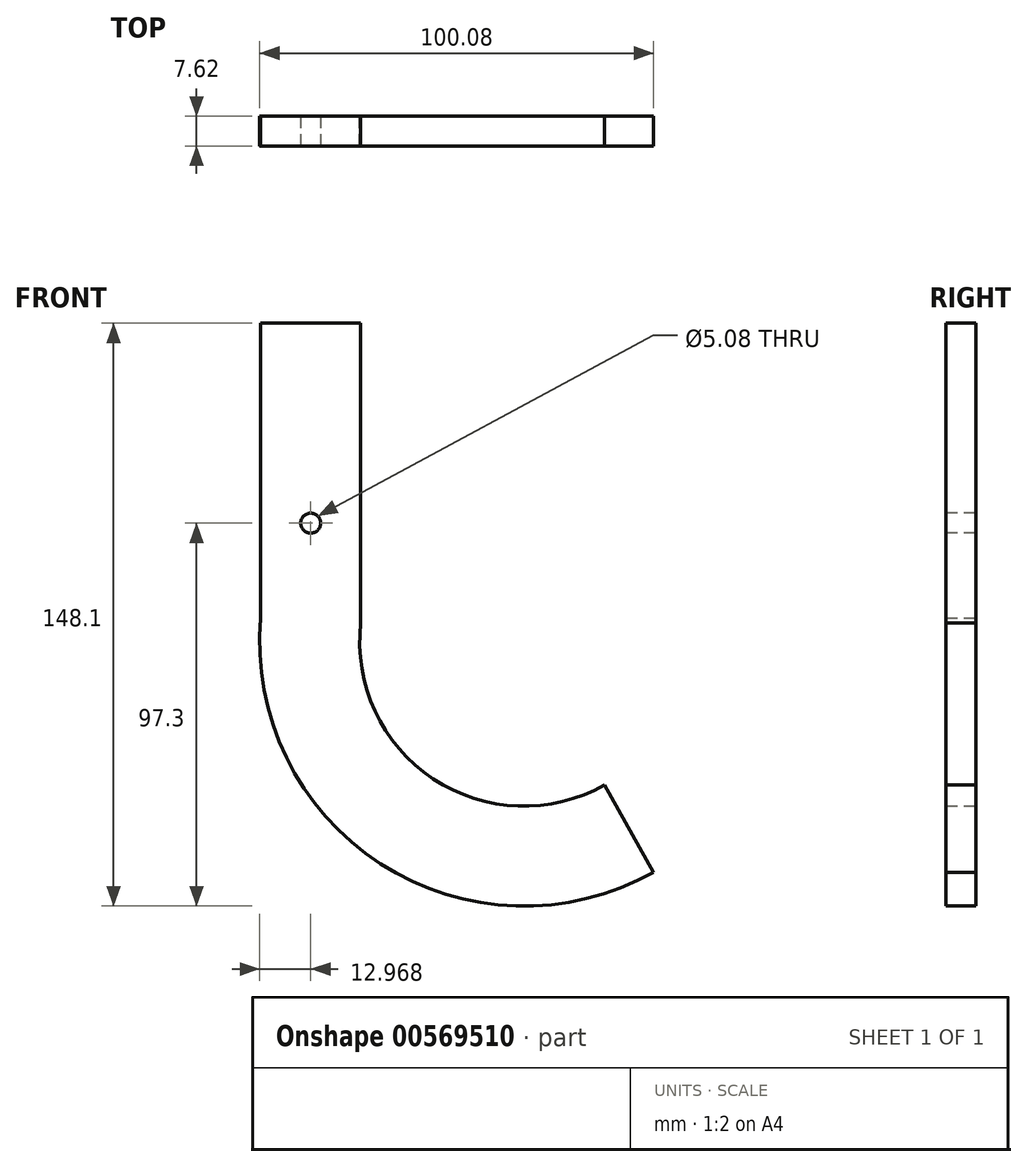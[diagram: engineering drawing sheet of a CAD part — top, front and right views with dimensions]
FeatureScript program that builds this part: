
annotation { "Feature Type Name" : "Feature", "Feature Type Description" : "" }
export const myFeature = defineFeature(function(context is Context, id is Id, definition is map)
    precondition{}
    {
        {
            var Q0;
            Q0=qCreatedBy(makeId("Front.planeOp"),FACE);
            var sketch = newSketch(context, id + "F0", { "sketchPlane" : qUnion([Q0])});
            skLineSegment(sketch, "E0", {"start": v(-8.68, 20.1) * mm, "end": v(-34.08, 20.1) * mm});
            skLineSegment(sketch, "E1.bottom", {"start": v(-34.08, 20.1) * mm, "end": v(-8.68, 20.1) * mm});
            skLineSegment(sketch, "E1.top", {"start": v(-34.08, 96.3) * mm, "end": v(-8.68, 96.3) * mm});
            skLineSegment(sketch, "E1.left", {"start": v(-34.08, 20.1) * mm, "end": v(-34.08, 96.3) * mm});
            skLineSegment(sketch, "E1.right", {"start": v(-8.68, 20.1) * mm, "end": v(-8.68, 96.3) * mm});
            skArc(sketch, "E2", {"start": v(-8.68, 20.1) * mm, "mid": v(9.71, -19.42) * mm, "end": v(53.29, -21.03) * mm});
            skArc(sketch, "E3.0", {"start": v(-33.92, 22.99) * mm, "mid": v(-4.34, -40.58) * mm, "end": v(65.73, -43.17) * mm});
            skLineSegment(sketch, "E4", {"start": v(53.29, -21.03) * mm, "end": v(65.73, -43.17) * mm});
            skSolve(sketch);
        }
        {
            var Q0;
            Q0 = qSketchRegion(id + "F0", true);
            extrude(context, id + "F1", {"entities" : qUnion([Q0]), "depth" : 7.62 * mm, "offsetDistance" : 25.4 * mm});
        }
        {
            var Q0;
            Q0=makeQuery(id+"F1.opExtrude","CAP_FACE",FACE,{"disambiguationData":[OSD([sQuery(id+"F0.wireOp",EDGE,"KNPuZlz0-q2br-hx0y-8LLM-wSXk275fcNS4"),sQuery(id+"F0.wireOp",EDGE,"8d5c5f95-3a9a-44d8-8a8f-d24cceffa02c"),sQuery(id+"F0.wireOp",EDGE,"c23f95d2-77ba-4bda-ba65-29fe8ec58674.0"),sQuery(id+"F0.wireOp",EDGE,"0ksrw0VH-sesD-FrQk-VRX6-Dm4IhUhtwqMp"),sQuery(id+"F0.wireOp",EDGE,"E1.top"),sQuery(id+"F0.wireOp",EDGE,"E1.left"),sQuery(id+"F0.wireOp",EDGE,"E1.right")])],"isStart":false});
            var sketch = newSketch(context, id + "F2", { "sketchPlane" : qUnion([Q0])});
            skPoint(sketch, "E5", {"position": v(-21.38, 45.5) * mm});
            skSolve(sketch);
        }
        {
            var Q0;
            Q0=sQuery(id+"F2.wireOp",VERTEX,"E5");
            var Q1;
            Q1=makeQuery(id+"F1.opExtrude","SWEPT_BODY",BODY,{"disambiguationData":[OSD([sQuery(id+"F0.wireOp",EDGE,"KNPuZlz0-q2br-hx0y-8LLM-wSXk275fcNS4"),sQuery(id+"F0.wireOp",EDGE,"8d5c5f95-3a9a-44d8-8a8f-d24cceffa02c"),sQuery(id+"F0.wireOp",EDGE,"c23f95d2-77ba-4bda-ba65-29fe8ec58674.0"),sQuery(id+"F0.wireOp",EDGE,"0ksrw0VH-sesD-FrQk-VRX6-Dm4IhUhtwqMp"),sQuery(id+"F0.wireOp",EDGE,"E1.top"),sQuery(id+"F0.wireOp",EDGE,"E1.left"),sQuery(id+"F0.wireOp",EDGE,"E1.right")])]});
            hole(context, id + "F3", {"style" : HoleStyle.SIMPLE, "endStyle" : HoleEndStyle.THROUGH, "holeDiameter" : 5.08 * mm, "isTappedThrough" : true, "tappedDepth" : 12.7 * mm, "tapClearance" : 3, "locations" : qUnion([Q0]), "scope" : qUnion([Q1])});
        }
    });
